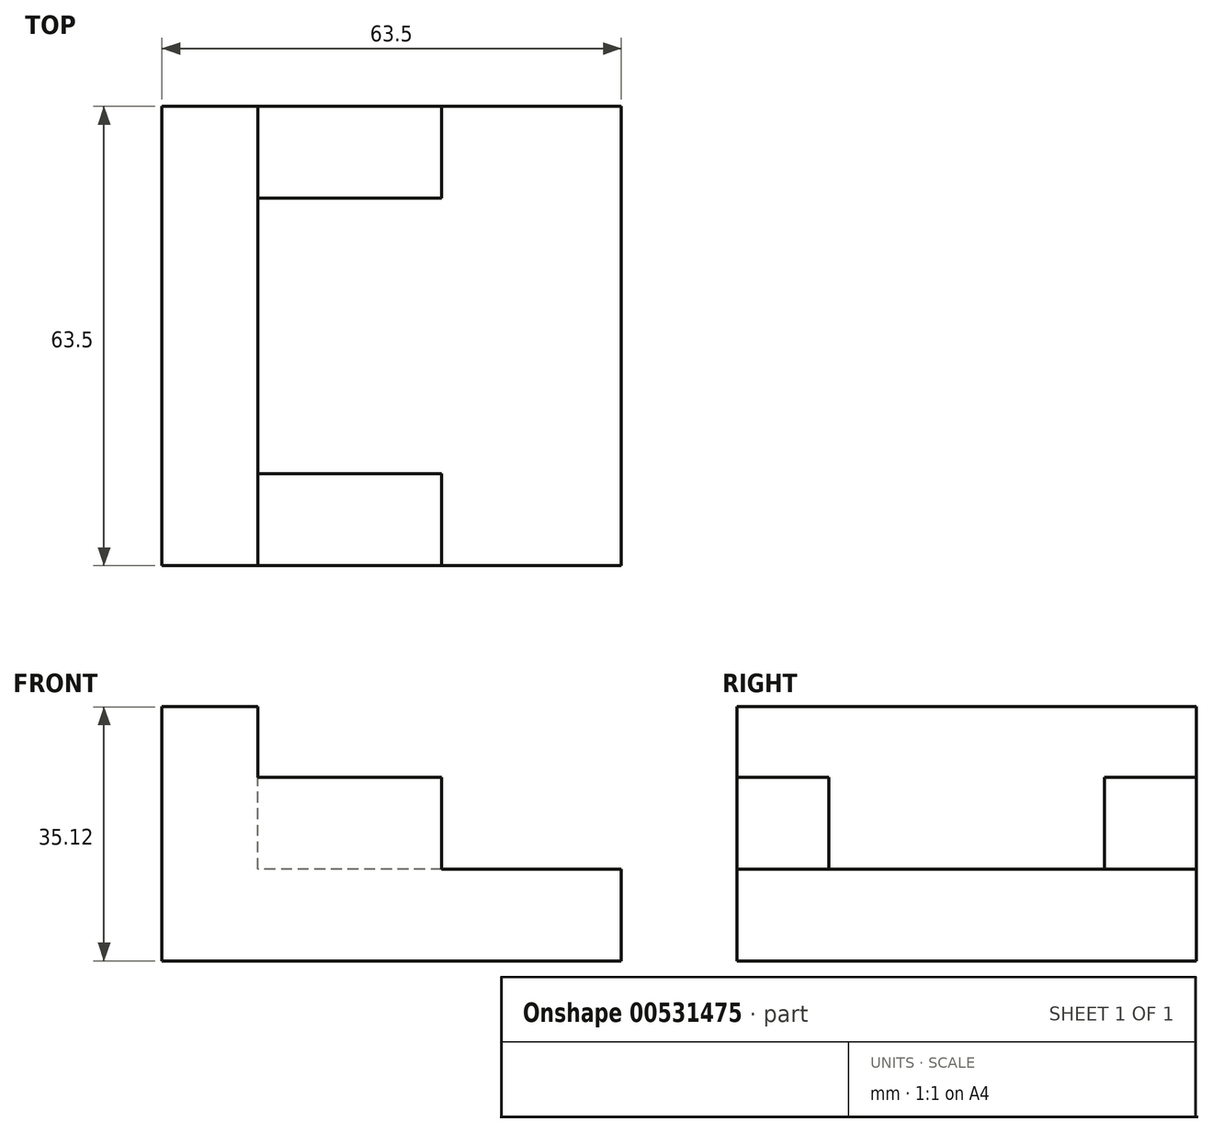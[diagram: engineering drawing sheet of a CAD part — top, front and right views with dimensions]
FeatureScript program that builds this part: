
annotation { "Feature Type Name" : "Feature", "Feature Type Description" : "" }
export const myFeature = defineFeature(function(context is Context, id is Id, definition is map)
    precondition{}
    {
        {
            var Q0;
            Q0=qCreatedBy(makeId("Front.planeOp"),FACE);
            var sketch = newSketch(context, id + "F0", { "sketchPlane" : qUnion([Q0])});
            skLineSegment(sketch, "E0.bottom", {"start": v(-37.75, 12.7) * mm, "end": v(25.75, 12.7) * mm});
            skLineSegment(sketch, "E0.top", {"start": v(-37.75, 0) * mm, "end": v(25.75, 0) * mm});
            skLineSegment(sketch, "E0.left", {"start": v(-37.75, 12.7) * mm, "end": v(-37.75, 0) * mm});
            skLineSegment(sketch, "E0.right", {"start": v(25.75, 12.7) * mm, "end": v(25.75, 0) * mm});
            skSolve(sketch);
        }
        {
            var Q0;
            Q0=makeQuery(id+"F0.imprint","IMPRINT",FACE,{"disambiguationData":[TD([[makeQuery(id+"F0.imprint","IMPRINT",EDGE,{"derivedFrom":sQuery(id+"F0.wireOp",EDGE,"E0.bottom")}),-1.0]])]});
            extrude(context, id + "F1", {"entities" : qUnion([Q0]), "depth" : 63.5 * mm, "offsetDistance" : 25.4 * mm});
        }
        {
            var Q0;
            Q0=qCreatedBy(makeId("Front.planeOp"),FACE);
            var sketch = newSketch(context, id + "F2", { "sketchPlane" : qUnion([Q0])});
            skLineSegment(sketch, "E1.bottom", {"start": v(-24.48, 35.12) * mm, "end": v(-37.75, 35.12) * mm});
            skLineSegment(sketch, "E1.top", {"start": v(-24.48, 12.7) * mm, "end": v(-37.75, 12.7) * mm});
            skLineSegment(sketch, "E1.left", {"start": v(-24.48, 35.12) * mm, "end": v(-24.48, 12.7) * mm});
            skLineSegment(sketch, "E1.right", {"start": v(-37.75, 35.12) * mm, "end": v(-37.75, 12.7) * mm});
            skSolve(sketch);
        }
        {
            var Q0;
            Q0=makeQuery(id+"F2.imprint","IMPRINT",FACE,{"disambiguationData":[TD([[makeQuery(id+"F2.imprint","IMPRINT",EDGE,{"derivedFrom":sQuery(id+"F2.wireOp",EDGE,"E1.bottom")}),1.0]])]});
            extrude(context, id + "F3", {"entities" : qUnion([Q0]), "operationType" : NewBodyOperationType.ADD, "depth" : 63.5 * mm, "offsetDistance" : 25.4 * mm});
        }
        {
            var Q0;
            Q0=makeQuery(id+"F3.opExtrude","SWEPT_FACE",FACE,{"disambiguationData":[OSD([sQuery(id+"F2.wireOp",EDGE,"E1.left")])]});
            var sketch = newSketch(context, id + "F4", { "sketchPlane" : qUnion([Q0])});
            skLineSegment(sketch, "E2.bottom", {"start": v(-63.5, 12.7) * mm, "end": v(-50.8, 12.7) * mm});
            skLineSegment(sketch, "E2.top", {"start": v(-63.5, 25.4) * mm, "end": v(-50.8, 25.4) * mm});
            skLineSegment(sketch, "E2.left", {"start": v(-63.5, 12.7) * mm, "end": v(-63.5, 25.4) * mm});
            skLineSegment(sketch, "E2.right", {"start": v(-50.8, 12.7) * mm, "end": v(-50.8, 25.4) * mm});
            skSolve(sketch);
        }
        {
            var Q0;
            Q0=makeQuery(id+"F4.imprint","IMPRINT",FACE,{"disambiguationData":[TD([[makeQuery(id+"F4.imprint","IMPRINT",EDGE,{"derivedFrom":sQuery(id+"F4.wireOp",EDGE,"E2.bottom")}),1.0]])]});
            extrude(context, id + "F5", {"entities" : qUnion([Q0]), "operationType" : NewBodyOperationType.ADD, "depth" : 25.4 * mm, "offsetDistance" : 25.4 * mm});
        }
        {
            var Q0;
            Q0=makeQuery(id+"F3.opExtrude","SWEPT_FACE",FACE,{"disambiguationData":[OSD([sQuery(id+"F2.wireOp",EDGE,"E1.left")])]});
            var sketch = newSketch(context, id + "F6", { "sketchPlane" : qUnion([Q0])});
            skLineSegment(sketch, "E3.bottom", {"start": v(0, 12.7) * mm, "end": v(-12.7, 12.7) * mm});
            skLineSegment(sketch, "E3.top", {"start": v(0, 25.4) * mm, "end": v(-12.7, 25.4) * mm});
            skLineSegment(sketch, "E3.left", {"start": v(0, 12.7) * mm, "end": v(0, 25.4) * mm});
            skLineSegment(sketch, "E3.right", {"start": v(-12.7, 12.7) * mm, "end": v(-12.7, 25.4) * mm});
            skSolve(sketch);
        }
        {
            var Q0;
            Q0=makeQuery(id+"F6.imprint","IMPRINT",FACE,{"disambiguationData":[TD([[makeQuery(id+"F6.imprint","IMPRINT",EDGE,{"derivedFrom":sQuery(id+"F6.wireOp",EDGE,"E3.bottom")}),1.0]])]});
            extrude(context, id + "F7", {"entities" : qUnion([Q0]), "operationType" : NewBodyOperationType.ADD, "depth" : 25.4 * mm, "offsetDistance" : 25.4 * mm});
        }
    });
